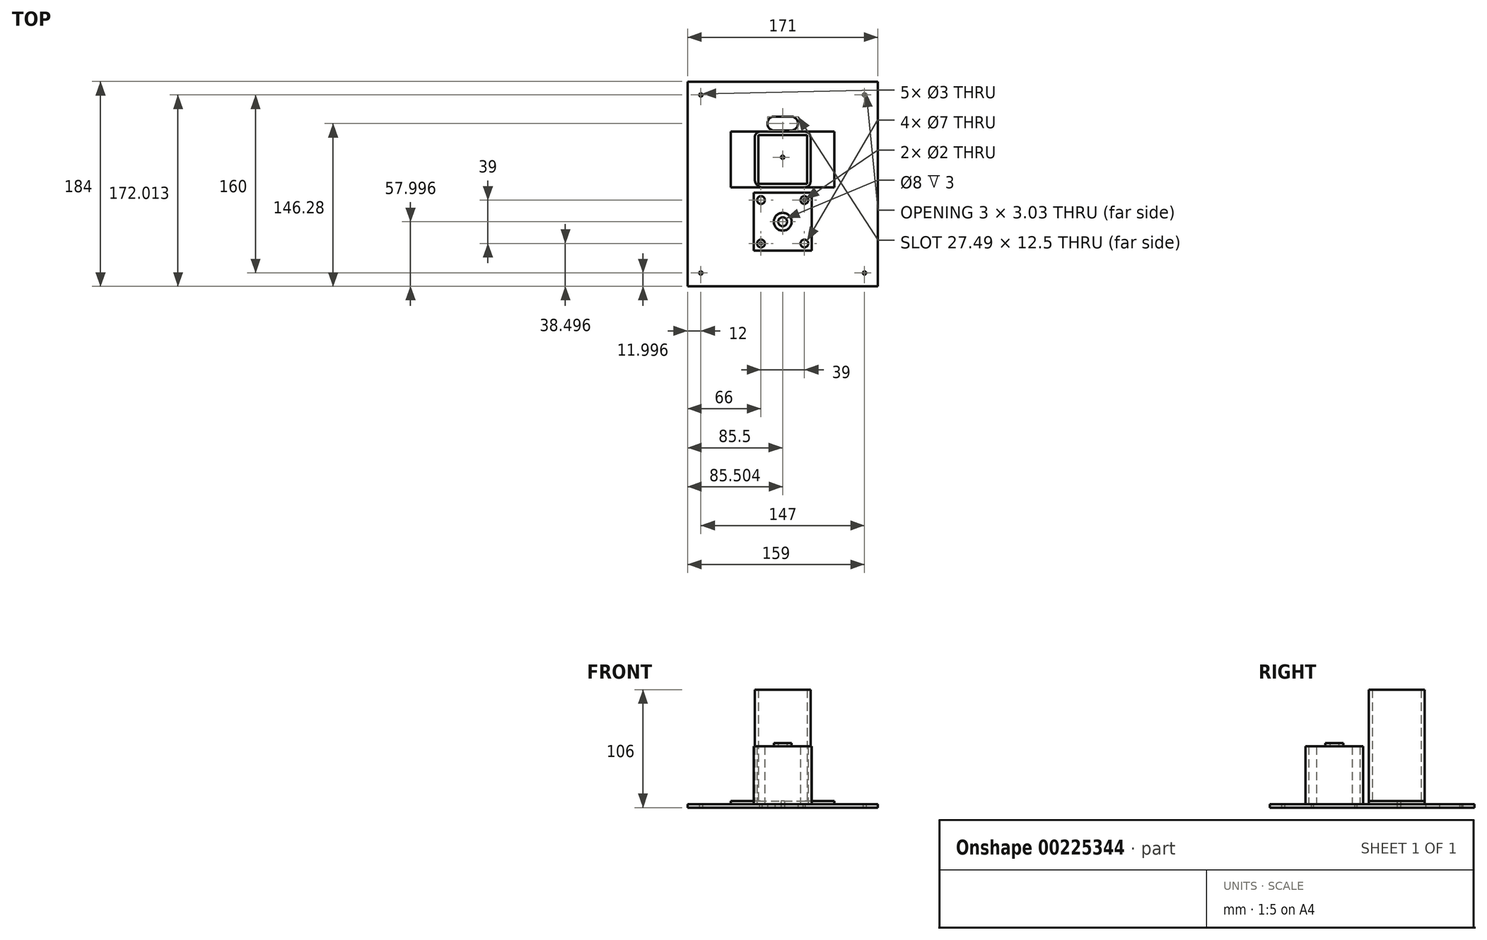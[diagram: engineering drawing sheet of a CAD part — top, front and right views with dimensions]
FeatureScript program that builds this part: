
annotation { "Feature Type Name" : "Feature", "Feature Type Description" : "" }
export const myFeature = defineFeature(function(context is Context, id is Id, definition is map)
    precondition{}
    {
        {
            var Q0;
            Q0=qCreatedBy(makeId("Top.planeOp"),FACE);
            var sketch = newSketch(context, id + "F0", { "sketchPlane" : qUnion([Q0])});
            skLineSegment(sketch, "E0.bottom", {"start": v(-95.96, 90.48) * mm, "end": v(75.04, 90.48) * mm});
            skLineSegment(sketch, "E0.top", {"start": v(-95.96, -93.52) * mm, "end": v(75.04, -93.52) * mm});
            skLineSegment(sketch, "E0.left", {"start": v(-95.96, 90.48) * mm, "end": v(-95.96, -93.52) * mm});
            skLineSegment(sketch, "E0.right", {"start": v(75.04, 90.48) * mm, "end": v(75.04, -93.52) * mm});
            skCircle(sketch, "E1", {"center": v(-17.96, 52.76) * mm, "radius": 6.25 * mm});
            skCircle(sketch, "E2", {"center": v(-2.96, 52.76) * mm, "radius": 6.25 * mm});
            skLineSegment(sketch, "E3", {"start": v(-17.96, 46.5) * mm, "end": v(-2.96, 46.5) * mm});
            skCircle(sketch, "E4", {"center": v(63.04, 78.5) * mm, "radius": 1.5 * mm});
            skCircle(sketch, "E5", {"center": v(63.04, 78.48) * mm, "radius": 1.5 * mm});
            skCircle(sketch, "E6", {"center": v(63.04, -81.52) * mm, "radius": 1.5 * mm});
            skCircle(sketch, "E7", {"center": v(-83.96, -81.52) * mm, "radius": 1.5 * mm});
            skLineSegment(sketch, "E8", {"start": v(63.04, -81.52) * mm, "end": v(63.04, -105.1) * mm, "construction": true});
            skCircle(sketch, "E9", {"center": v(-83.96, 78.48) * mm, "radius": 1.5 * mm});
            skLineSegment(sketch, "E10", {"start": v(-18.6, 58.98) * mm, "end": v(-2.96, 59) * mm});
            skSolve(sketch);
        }
        {
            var Q0;
            Q0 = qSketchRegion(id + "F0", true);
            extrude(context, id + "F1", {"entities" : qUnion([Q0]), "depth" : 3 * mm, "offsetDistance" : 25 * mm});
        }
        {
            var Q0;
            Q0=makeQuery(id+"F1.opExtrude","CAP_FACE",FACE,{"disambiguationData":[OSD([sQuery(id+"F0.wireOp",EDGE,"E0.bottom"),sQuery(id+"F0.wireOp",EDGE,"E0.top"),sQuery(id+"F0.wireOp",EDGE,"E0.left"),sQuery(id+"F0.wireOp",EDGE,"E0.right"),sQuery(id+"F0.wireOp",EDGE,"E1"),sQuery(id+"F0.wireOp",EDGE,"E2"),sQuery(id+"F0.wireOp",EDGE,"E4"),sQuery(id+"F0.wireOp",EDGE,"E5"),sQuery(id+"F0.wireOp",EDGE,"E6"),sQuery(id+"F0.wireOp",EDGE,"E7"),sQuery(id+"F0.wireOp",EDGE,"E9")])],"isStart":false});
            var sketch = newSketch(context, id + "F2", { "sketchPlane" : qUnion([Q0])});
            skLineSegment(sketch, "E11.bottom", {"start": v(-56.96, 45.48) * mm, "end": v(36.04, 45.48) * mm});
            skLineSegment(sketch, "E11.top", {"start": v(-56.96, -4.52) * mm, "end": v(36.04, -4.52) * mm});
            skLineSegment(sketch, "E11.left", {"start": v(-56.96, 45.48) * mm, "end": v(-56.96, -4.52) * mm});
            skLineSegment(sketch, "E11.right", {"start": v(36.04, 45.48) * mm, "end": v(36.04, -4.52) * mm});
            skLineSegment(sketch, "E12", {"start": v(-56.96, -4.52) * mm, "end": v(-114.45, -4.52) * mm, "construction": true});
            skSolve(sketch);
        }
        {
            var Q0;
            Q0=makeQuery(id+"F2.imprint","IMPRINT",FACE,{"disambiguationData":[TD([[makeQuery(id+"F2.imprint","IMPRINT",EDGE,{"derivedFrom":sQuery(id+"F2.wireOp",EDGE,"E11.bottom")}),-1.0]])]});
            extrude(context, id + "F3", {"entities" : qUnion([Q0]), "depth" : 3 * mm, "offsetDistance" : 25 * mm});
        }
        {
            var Q0;
            Q0=makeQuery(id+"F3.opExtrude","CAP_FACE",FACE,{"disambiguationData":[OSD([sQuery(id+"F2.wireOp",EDGE,"E11.bottom"),sQuery(id+"F2.wireOp",EDGE,"E11.top"),sQuery(id+"F2.wireOp",EDGE,"E11.left"),sQuery(id+"F2.wireOp",EDGE,"E11.right")])],"isStart":false});
            var sketch = newSketch(context, id + "F4", { "sketchPlane" : qUnion([Q0])});
            skLineSegment(sketch, "E13", {"start": v(-35.46, 40.48) * mm, "end": v(-35.46, 1.98) * mm});
            skLineSegment(sketch, "E14", {"start": v(14.54, 40.48) * mm, "end": v(14.54, 0.48) * mm});
            skLineSegment(sketch, "E15", {"start": v(-28.96, -4.52) * mm, "end": v(9.54, -4.52) * mm});
            skLineSegment(sketch, "E16", {"start": v(-30.46, 45.48) * mm, "end": v(9.54, 45.48) * mm});
            skLineSegment(sketch, "E17.0", {"start": v(-32.46, 42.48) * mm, "end": v(-32.46, -1.52) * mm});
            skLineSegment(sketch, "E17.1", {"start": v(-32.46, 42.48) * mm, "end": v(11.54, 42.48) * mm});
            skLineSegment(sketch, "E17.2", {"start": v(11.54, 42.48) * mm, "end": v(11.54, -1.52) * mm});
            skLineSegment(sketch, "E17.3", {"start": v(-32.46, -1.52) * mm, "end": v(11.54, -1.52) * mm});
            skLineSegment(sketch, "E18.0", {"start": v(-61.96, 50.48) * mm, "end": v(-61.96, -9.52) * mm});
            skLineSegment(sketch, "E18.1", {"start": v(41.04, 50.48) * mm, "end": v(-61.96, 50.48) * mm});
            skLineSegment(sketch, "E18.2", {"start": v(41.04, -9.52) * mm, "end": v(41.04, 50.48) * mm});
            skLineSegment(sketch, "E18.3", {"start": v(-61.96, -9.52) * mm, "end": v(41.04, -9.52) * mm});
            skPoint(sketch, "E19.visualSharp", {"position": v(-35.46, 45.48) * mm});
            skArc(sketch, "E19.filletArc", {"start": v(-30.46, 45.48) * mm, "mid": v(-34, 44.01) * mm, "end": v(-35.46, 40.48) * mm});
            skPoint(sketch, "E20.visualSharp", {"position": v(14.54, -4.52) * mm});
            skArc(sketch, "E20.filletArc", {"start": v(9.54, -4.52) * mm, "mid": v(13.08, -3.06) * mm, "end": v(14.54, 0.48) * mm});
            skPoint(sketch, "E21.visualSharp", {"position": v(14.54, 45.48) * mm});
            skArc(sketch, "E21.filletArc", {"start": v(14.54, 40.48) * mm, "mid": v(13.08, 44.01) * mm, "end": v(9.54, 45.48) * mm});
            skPoint(sketch, "E22.visualSharp", {"position": v(-35.46, -4.52) * mm});
            skArc(sketch, "E22.filletArc", {"start": v(-35.46, 1.98) * mm, "mid": v(-33.56, -2.62) * mm, "end": v(-28.96, -4.52) * mm});
            skSolve(sketch);
        }
        {
            var Q0;
            Q0=makeQuery(id+"F4.imprint","IMPRINT",FACE,{"disambiguationData":[TD([[makeQuery(id+"F4.imprint","IMPRINT",EDGE,{"derivedFrom":sQuery(id+"F4.wireOp",EDGE,"E13")}),1.0]])]});
            extrude(context, id + "F5", {"entities" : qUnion([Q0]), "operationType" : NewBodyOperationType.ADD, "depth" : 100 * mm, "offsetDistance" : 25 * mm});
        }
        {
            var Q0;
            Q0=makeQuery(id+"F1.opExtrude","CAP_FACE",FACE,{"disambiguationData":[OSD([sQuery(id+"F0.wireOp",EDGE,"E0.bottom"),sQuery(id+"F0.wireOp",EDGE,"E0.top"),sQuery(id+"F0.wireOp",EDGE,"E0.left"),sQuery(id+"F0.wireOp",EDGE,"E0.right"),sQuery(id+"F0.wireOp",EDGE,"E1"),sQuery(id+"F0.wireOp",EDGE,"E2"),sQuery(id+"F0.wireOp",EDGE,"E4"),sQuery(id+"F0.wireOp",EDGE,"E5"),sQuery(id+"F0.wireOp",EDGE,"E6"),sQuery(id+"F0.wireOp",EDGE,"E7"),sQuery(id+"F0.wireOp",EDGE,"E9")])],"isStart":false});
            var sketch = newSketch(context, id + "F6", { "sketchPlane" : qUnion([Q0])});
            skLineSegment(sketch, "E23.bottom", {"start": v(-36.46, -9.52) * mm, "end": v(15.54, -9.52) * mm});
            skLineSegment(sketch, "E23.top", {"start": v(-36.46, -61.52) * mm, "end": v(15.54, -61.52) * mm});
            skLineSegment(sketch, "E23.left", {"start": v(-36.46, -9.52) * mm, "end": v(-36.46, -61.52) * mm});
            skLineSegment(sketch, "E23.right", {"start": v(15.54, -9.52) * mm, "end": v(15.54, -61.52) * mm});
            skCircle(sketch, "E24", {"center": v(-29.96, -16.02) * mm, "radius": 3.5 * mm});
            skCircle(sketch, "E25", {"center": v(9.04, -16.02) * mm, "radius": 3.5 * mm});
            skCircle(sketch, "E26", {"center": v(-29.96, -55.02) * mm, "radius": 3.5 * mm});
            skCircle(sketch, "E27", {"center": v(9.04, -55.02) * mm, "radius": 3.5 * mm});
            skCircle(sketch, "E28", {"center": v(-10.46, -35.52) * mm, "radius": 8 * mm});
            skSolve(sketch);
        }
        {
            var Q0;
            Q0=makeQuery(id+"F6.imprint","IMPRINT",FACE,{"disambiguationData":[TD([[makeQuery(id+"F6.imprint","IMPRINT",EDGE,{"derivedFrom":sQuery(id+"F6.wireOp",EDGE,"E23.bottom")}),-1.0]])]});
            var Q1;
            Q1=makeQuery(id+"F6.imprint","IMPRINT",FACE,{"disambiguationData":[TD([[makeQuery(id+"F6.imprint","IMPRINT",EDGE,{"derivedFrom":sQuery(id+"F6.wireOp",EDGE,"E28")}),1.0]])]});
            extrude(context, id + "F7", {"entities" : qUnion([Q0, Q1]), "depth" : 52 * mm, "offsetDistance" : 25 * mm});
        }
        {
            var Q0;
            Q0=makeQuery(id+"F7.opExtrude","CAP_FACE",FACE,{"disambiguationData":[OSD([sQuery(id+"F6.wireOp",EDGE,"E23.bottom"),sQuery(id+"F6.wireOp",EDGE,"E23.top"),sQuery(id+"F6.wireOp",EDGE,"E23.left"),sQuery(id+"F6.wireOp",EDGE,"E23.right"),sQuery(id+"F6.wireOp",EDGE,"E24"),sQuery(id+"F6.wireOp",EDGE,"E25"),sQuery(id+"F6.wireOp",EDGE,"E26"),sQuery(id+"F6.wireOp",EDGE,"E27")])],"isStart":false});
            var sketch = newSketch(context, id + "F8", { "sketchPlane" : qUnion([Q0])});
            skCircle(sketch, "E29", {"center": v(-10.46, -35.52) * mm, "radius": 8 * mm});
            skCircle(sketch, "E30", {"center": v(-10.46, -35.52) * mm, "radius": 4 * mm});
            skSolve(sketch);
        }
        {
            var Q0;
            Q0 = qSketchRegion(id + "F8", true);
            extrude(context, id + "F9", {"entities" : qUnion([Q0]), "operationType" : NewBodyOperationType.ADD, "depth" : 3 * mm, "offsetDistance" : 25 * mm});
        }
        {
            var Q0;
            {var subQ0=sQuery(id+"F6.wireOp",EDGE,"E23.left");var subQ1=sQuery(id+"F6.wireOp",EDGE,"E23.top");var subQ2=sQuery(id+"F6.wireOp",EDGE,"E23.right");var subQ3=sQuery(id+"F6.wireOp",EDGE,"E23.bottom");var subQ4=sQuery(id+"F6.wireOp",EDGE,"E24");var subQ5=sQuery(id+"F6.wireOp",EDGE,"E25");var subQ6=sQuery(id+"F6.wireOp",EDGE,"E26");var subQ7=sQuery(id+"F6.wireOp",EDGE,"E27");Q0=makeQuery(id+"F9.boolean.opBoolean","SPLIT",FACE,{"disambiguationData":[TD([makeQuery(id+"F7.opExtrude","SWEPT_FACE",FACE,{"disambiguationData":[OSD([subQ3])]})])],"derivedFrom":makeQuery(id+"F7.opExtrude","CAP_FACE",FACE,{"disambiguationData":[OSD([subQ3,subQ1,subQ0,subQ2,subQ4,subQ5,subQ6,subQ7])],"isStart":false})});}
            var sketch = newSketch(context, id + "F10", { "sketchPlane" : qUnion([Q0])});
            skCircle(sketch, "E31", {"center": v(-29.96, -16.02) * mm, "radius": 1 * mm});
            skCircle(sketch, "E32", {"center": v(9.04, -16.02) * mm, "radius": 1 * mm});
            skCircle(sketch, "E33", {"center": v(9.04, -55.02) * mm, "radius": 1 * mm});
            skCircle(sketch, "E34", {"center": v(-29.96, -55.02) * mm, "radius": 1 * mm});
            skSolve(sketch);
        }
        {
            var Q0;
            Q0=makeQuery(id+"F10.imprint","IMPRINT",FACE,{"disambiguationData":[TD([[makeQuery(id+"F10.imprint","IMPRINT",EDGE,{"derivedFrom":sQuery(id+"F10.wireOp",EDGE,"E32")}),1.0]])]});
            var Q1;
            Q1=makeQuery(id+"F10.imprint","IMPRINT",FACE,{"disambiguationData":[TD([[makeQuery(id+"F10.imprint","IMPRINT",EDGE,{"derivedFrom":sQuery(id+"F10.wireOp",EDGE,"E34")}),1.0]])]});
            extrude(context, id + "F11", {"entities" : qUnion([Q0, Q1]), "operationType" : NewBodyOperationType.REMOVE, "endBound" : BoundingType.THROUGH_ALL, "oppositeDirection" : true, "depth" : 25 * mm, "offsetDistance" : 25 * mm});
        }
        {
            var Q0;
            Q0=makeQuery(id+"F1.opExtrude","CAP_FACE",FACE,{"disambiguationData":[OSD([sQuery(id+"F0.wireOp",EDGE,"E0.bottom"),sQuery(id+"F0.wireOp",EDGE,"E0.top"),sQuery(id+"F0.wireOp",EDGE,"E0.left"),sQuery(id+"F0.wireOp",EDGE,"E0.right"),sQuery(id+"F0.wireOp",EDGE,"E1"),sQuery(id+"F0.wireOp",EDGE,"E2"),sQuery(id+"F0.wireOp",EDGE,"E4"),sQuery(id+"F0.wireOp",EDGE,"E5"),sQuery(id+"F0.wireOp",EDGE,"E6"),sQuery(id+"F0.wireOp",EDGE,"E7"),sQuery(id+"F0.wireOp",EDGE,"E9")])],"isStart":true});
            var sketch = newSketch(context, id + "F12", { "sketchPlane" : qUnion([Q0])});
            skCircle(sketch, "E35", {"center": v(-10.46, -22.48) * mm, "radius": 1.5 * mm});
            skSolve(sketch);
        }
        {
            var Q0;
            Q0 = qSketchRegion(id + "F12", true);
            extrude(context, id + "F13", {"entities" : qUnion([Q0]), "operationType" : NewBodyOperationType.REMOVE, "endBound" : BoundingType.THROUGH_ALL, "oppositeDirection" : true, "depth" : 25 * mm, "offsetDistance" : 25 * mm});
        }
    });
